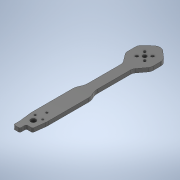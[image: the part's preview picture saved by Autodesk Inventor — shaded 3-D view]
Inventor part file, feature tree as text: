
AUTODESK INVENTOR PART (.ipt)
format: ipt  version: 2020 (Build 240168000, 168)  size: 249,344 bytes
history: native  units: in
note: dims shown in document units (in); Inventor stores cm internally (conversion verified against a paired STEP export)
features: sketch x3, extrude x2, fillet x2
ambient origin geometry x8: Origin, YZ Plane, XZ Plane, XY Plane, X Axis, Y Axis, Z Axis, Center Point
bodies: Body1 (feature_tree)
feature tree (7):
  extrude  "Extrusion1"  Depth=0.2362in
  sketch  "Sketch4"  dims[d7=0.4724in d9=7.0in d10=6.8898in d11=6.8898in]
  extrude  "Extrusion2"  Depth=7.0in
  fillet  "Fillet2"  Radius=6.8898in
  fillet  "Fillet3"  Radius=6.8898in
  sketch  "Sketch3"  dims[d2=0.2362in d3=0.0in d4=0.8352in]
  sketch  "Sketch5"  dims[d12=0.2992in d13=0.2992in d14=0.9835in d15=0.9835in d16=0.9835in d17=0.1181in d18=0.0in d20=0.3937in d21=0.7874in]
